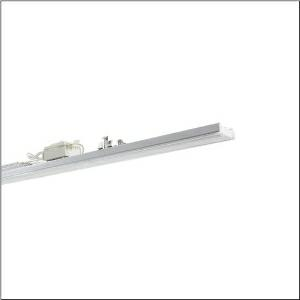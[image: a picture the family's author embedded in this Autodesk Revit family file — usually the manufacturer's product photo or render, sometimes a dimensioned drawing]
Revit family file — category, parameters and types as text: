
# Revit family: licross_r__21_recessed_ho_52tl1wmn4fxm_673f
name_source: partatom
category: Lighting Fixtures
units: mm (PartAtom-declared; Revit-internal decimal feet)

## family parameters
Cut with Voids When Loaded = No
Host = Face
Light Source = No
Part Type = Normal
Room Calculation Point = No
Round Connector Dimension = Use Diameter
Shared = No

## types (1)
- --- (1 x LED, 15140 lm, 83.1 W, 4000K)
    Apparent Load = 83 VA
    CIE Flux Codes = 73 94 99 100 100
    Color Rendering = 80
    Color Temperature = 4000K
    Default Elevation = 1800 mm
    Description = Licross® 21 Recessed HO, luminaire insert, of sheet steel, galvanised, coil coated, white, length: 1.500mm, width: 66mm, height: 67mm, LED rated luminous flux: 15.140lm, light colour: 840, control gear: ON/OFF Multilumen, with plug, 3-pole, with phase selection, mains connection: 220..240V, AC, 50/60Hz, rated input power: 83W, halogen-free wiring, primary optical cover: cover, of PMMA, light emission: direct distribution, primary light characteristic: symmetric, protection rating (complete): IP40, insulation class (complete): insulation class I (protective earthing), certification: CE, ENEC, VDE, UKCA, protection symbol: D if used in an environment without relevant dust loads with corresponding accessories, impact resistance: IK06, permissible ambient temperature for indoor applications: -35..+30°C, corresponds to IFS (International Featured Standards) requirements for safety and quality in the food industry, reducing of maximum allowable ambient temperature of 5°C with ceiling mounting, LABS conformity tested according to VDMA 24364:2018-05, packaging unit: 1 piece
    Height = 58 mm
    Lamp = 1 x LED
    Lamp Light Flux = 15140 lm
    Lamp Power = 83.1 W
    Lamp count = 1
    Length = 1500 mm
    Luminous efficacy = 182 lm/W
    Manufacturer = Siteco
    ModVariant = No
    Model = 52TL1WMN4FXM
    Mounting Place = Ceiling
    Mounting Type = Pendant
    Number of Poles = 1
    OnlyDefault = Yes
    Power Factor = 1
    Product Name = Licross® 21 Recessed HO
    Product group = luminaire insert
    ProductGroupID = 902
    Protection Class = Protection class I
    Protection Degree = IP 40
    RLX_Detail_Level = 1
    RLX_Emergency_Light_Flux = 0 lm
    RLX_Emergency_Type = 0
    RLX_Emergency_Type_DB = No
    RlxData = <blob elided: 22225 chars, md5=b541d4e0>
    Socket = socket
    Standby Power = 0 W
    System Light Flux = 15140 lm
    System Power = 83 W
    Type Comments = factory setting: luminous flux: 100 % | (A | C | E) | 195 mA
    Type Image = l_1296930.jpg
    URL = http://relux.com
    VarID = @adj_060182
    Voltage = 0 V
    Weight = 0.00 kg
    Width = 66 mm

## geometry (parser evidence)
native form markers: Blend x4, Sweep x11
no freeform markers — native parametric forms only
